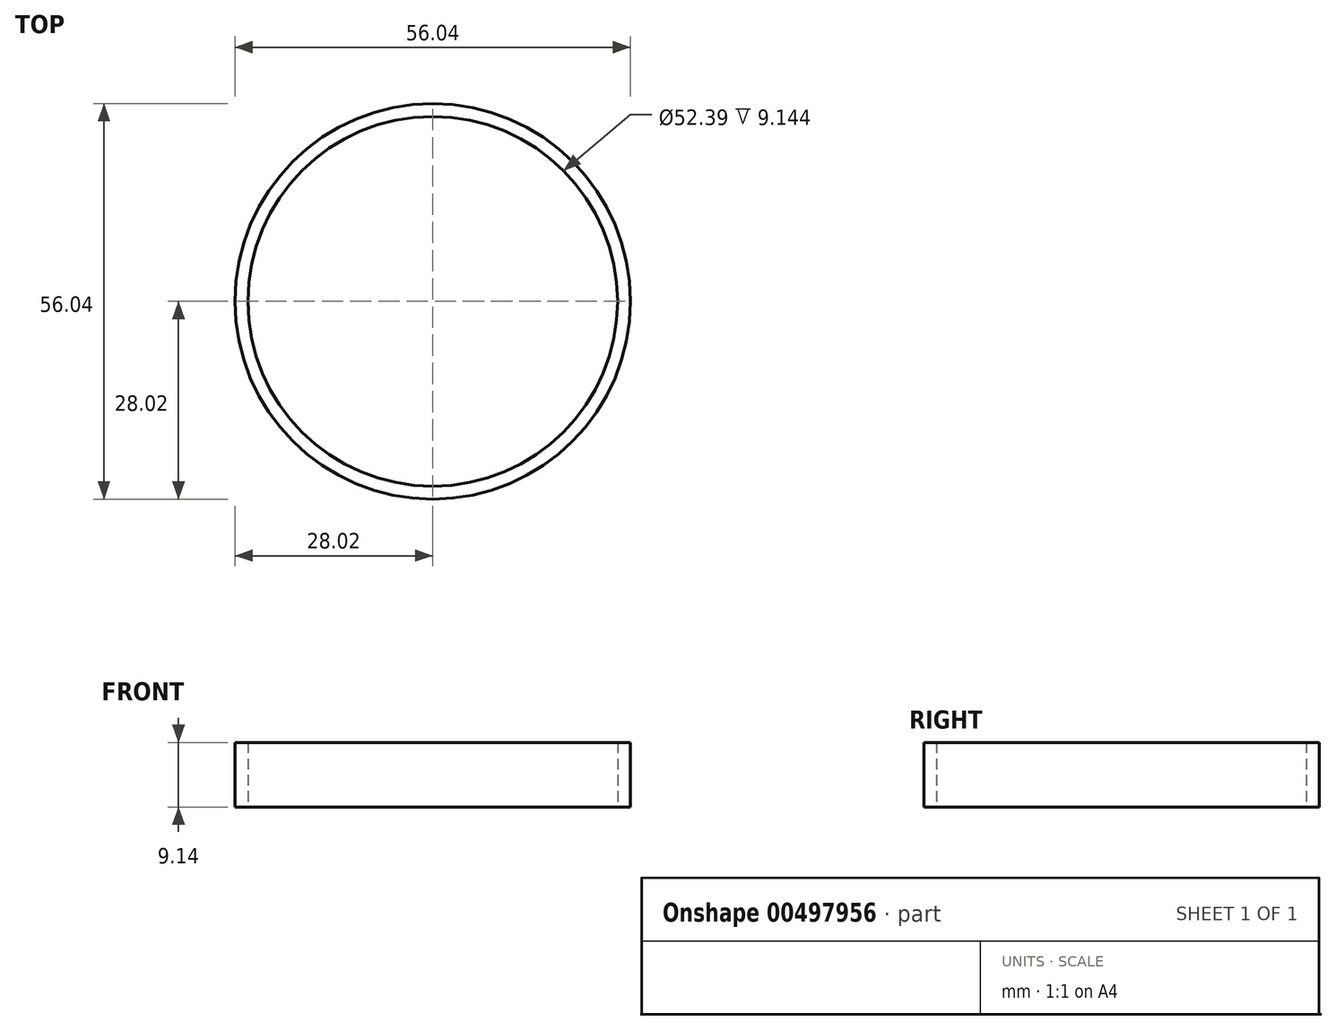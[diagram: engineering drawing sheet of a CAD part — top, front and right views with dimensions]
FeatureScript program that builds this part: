
annotation { "Feature Type Name" : "Feature", "Feature Type Description" : "" }
export const myFeature = defineFeature(function(context is Context, id is Id, definition is map)
    precondition{}
    {
        {
            var Q0;
            Q0=qCreatedBy(makeId("Top.planeOp"),FACE);
            var sketch = newSketch(context, id + "F0", { "sketchPlane" : qUnion([Q0])});
            skCircle(sketch, "E0", {"center": v(0, 0) * mm, "radius": 26.2 * mm});
            skSolve(sketch);
        }
        {
            var Q0;
            Q0=qCreatedBy(makeId("Top.planeOp"),FACE);
            cPlane(context, id + "F1", {"entities" : qUnion([Q0]), "cplaneType" : CPlaneType.OFFSET, "offset" : 9.14 * mm, "width" : 152.4 * mm, "height" : 152.4 * mm});
        }
        {
            var Q0;
            Q0=qCreatedBy(makeId("Top.planeOp"),FACE);
            var sketch = newSketch(context, id + "F2", { "sketchPlane" : qUnion([Q0])});
            skCircle(sketch, "E1", {"center": v(0, 0) * mm, "radius": 28 * mm});
            skSolve(sketch);
        }
        {
            var Q0;
            Q0=qCreatedBy(id+"F1.planeOp",FACE);
            var sketch = newSketch(context, id + "F3", { "sketchPlane" : qUnion([Q0])});
            skCircle(sketch, "E2", {"center": v(0, 0) * mm, "radius": 28.02 * mm});
            skSolve(sketch);
        }
        {
            var Q0;
            Q0=makeQuery(id+"F3.imprint","IMPRINT",FACE,{"disambiguationData":[TD([[makeQuery(id+"F3.imprint","IMPRINT",EDGE,{"derivedFrom":sQuery(id+"F3.wireOp",EDGE,"E2")}),1.0]])]});
            var Q1;
            Q1=makeQuery(id+"F2.imprint","IMPRINT",FACE,{"disambiguationData":[TD([[makeQuery(id+"F2.imprint","IMPRINT",EDGE,{"derivedFrom":sQuery(id+"F2.wireOp",EDGE,"E1")}),1.0]])]});
            loft(context, id + "F4", {"sheetProfilesArray" : [{ "sheetProfileEntities" : qUnion([Q0]) }, { "sheetProfileEntities" : qUnion([Q1]) }]});
        }
        {
            var Q0;
            Q0=makeQuery(id+"F0.imprint","IMPRINT",FACE,{"disambiguationData":[TD([[makeQuery(id+"F0.imprint","IMPRINT",EDGE,{"derivedFrom":sQuery(id+"F0.wireOp",EDGE,"E0")}),1.0]])]});
            var Q1;
            Q1=sQuery(id+"F0.wireOp",EDGE,"E0");
            extrude(context, id + "F5", {"entities" : qUnion([Q0]), "operationType" : NewBodyOperationType.REMOVE, "surfaceEntities" : qUnion([Q1]), "depth" : 25.9 * mm});
        }
    });
